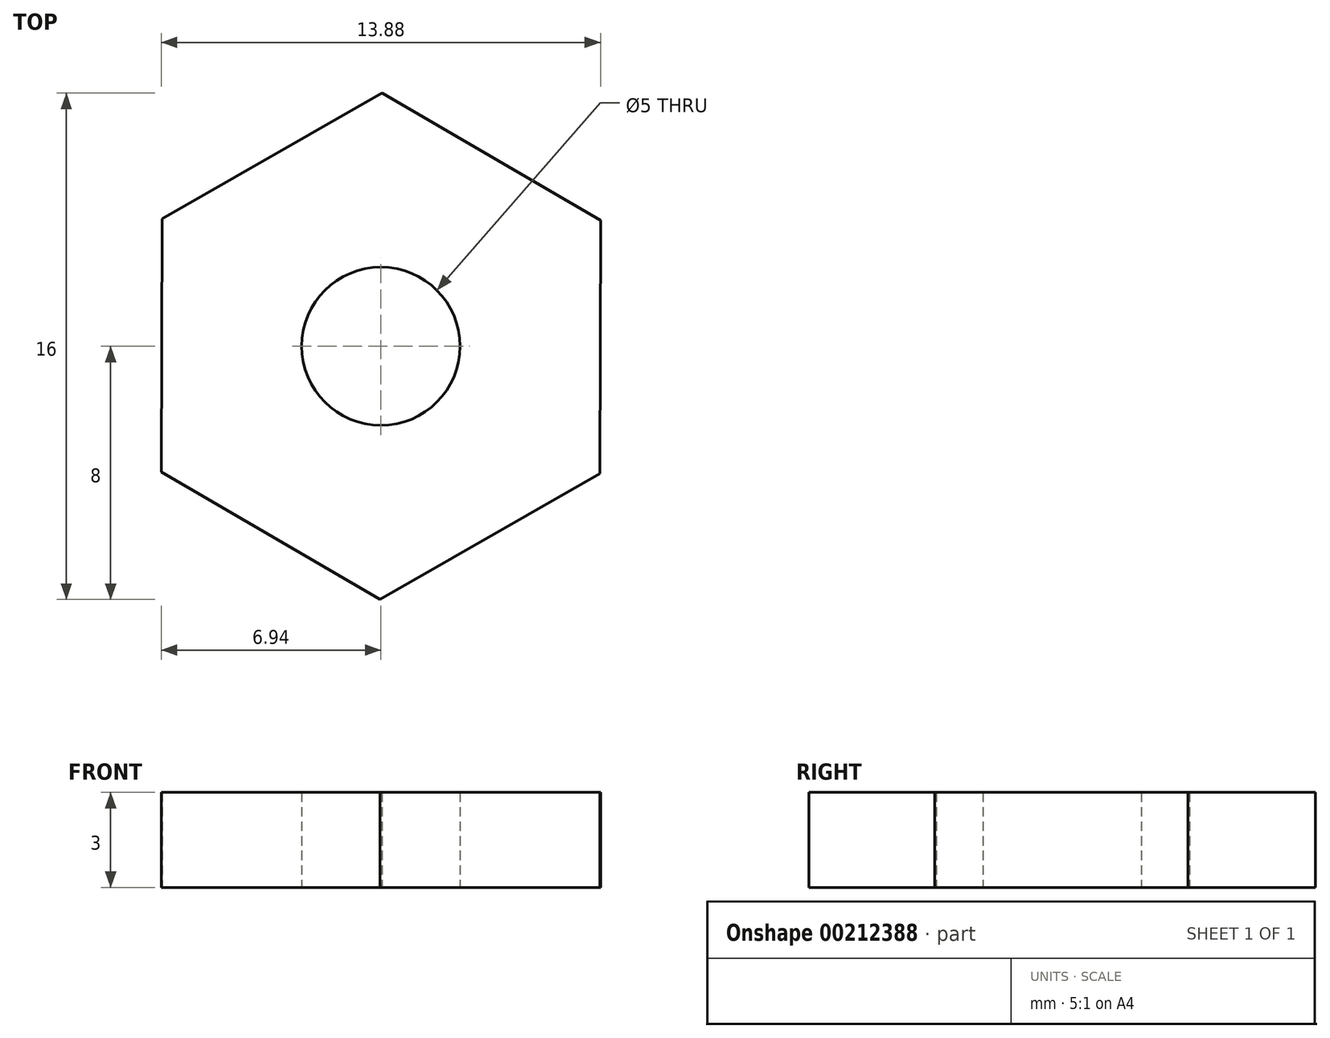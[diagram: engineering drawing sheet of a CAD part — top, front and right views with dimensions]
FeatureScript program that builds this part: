
annotation { "Feature Type Name" : "Feature", "Feature Type Description" : "" }
export const myFeature = defineFeature(function(context is Context, id is Id, definition is map)
    precondition{}
    {
        {
            var Q0;
            Q0=qCreatedBy(makeId("Top.planeOp"),FACE);
            var sketch = newSketch(context, id + "F0", { "sketchPlane" : qUnion([Q0])});
            skCircle(sketch, "E0", {"center": v(0, 0) * mm, "radius": 2.5 * mm});
            skCircle(sketch, "E1.cCircle", {"center": v(0, 0) * mm, "radius": 6.93 * mm, "construction": true});
            skLineSegment(sketch, "E1.0", {"start": v(-6.91, 4.03) * mm, "end": v(0.03, 8) * mm});
            skLineSegment(sketch, "E1.1", {"start": v(0.03, 8) * mm, "end": v(6.94, 3.97) * mm});
            skLineSegment(sketch, "E1.2", {"start": v(6.94, 3.97) * mm, "end": v(6.91, -4.03) * mm});
            skLineSegment(sketch, "E1.3", {"start": v(6.91, -4.03) * mm, "end": v(-0.03, -8) * mm});
            skLineSegment(sketch, "E1.4", {"start": v(-0.03, -8) * mm, "end": v(-6.94, -3.97) * mm});
            skLineSegment(sketch, "E1.5", {"start": v(-6.94, -3.97) * mm, "end": v(-6.91, 4.03) * mm});
            skPoint(sketch, "E1.0.midPoint", {"position": v(-3.44, 6.01) * mm});
            skSolve(sketch);
        }
        {
            var Q0;
            Q0=makeQuery(id+"F0.imprint","IMPRINT",FACE,{"disambiguationData":[TD([[makeQuery(id+"F0.imprint","IMPRINT",EDGE,{"derivedFrom":sQuery(id+"F0.wireOp",EDGE,"E0")}),-1.0]])]});
            extrude(context, id + "F1", {"entities" : qUnion([Q0]), "depth" : 3 * mm});
        }
    });
